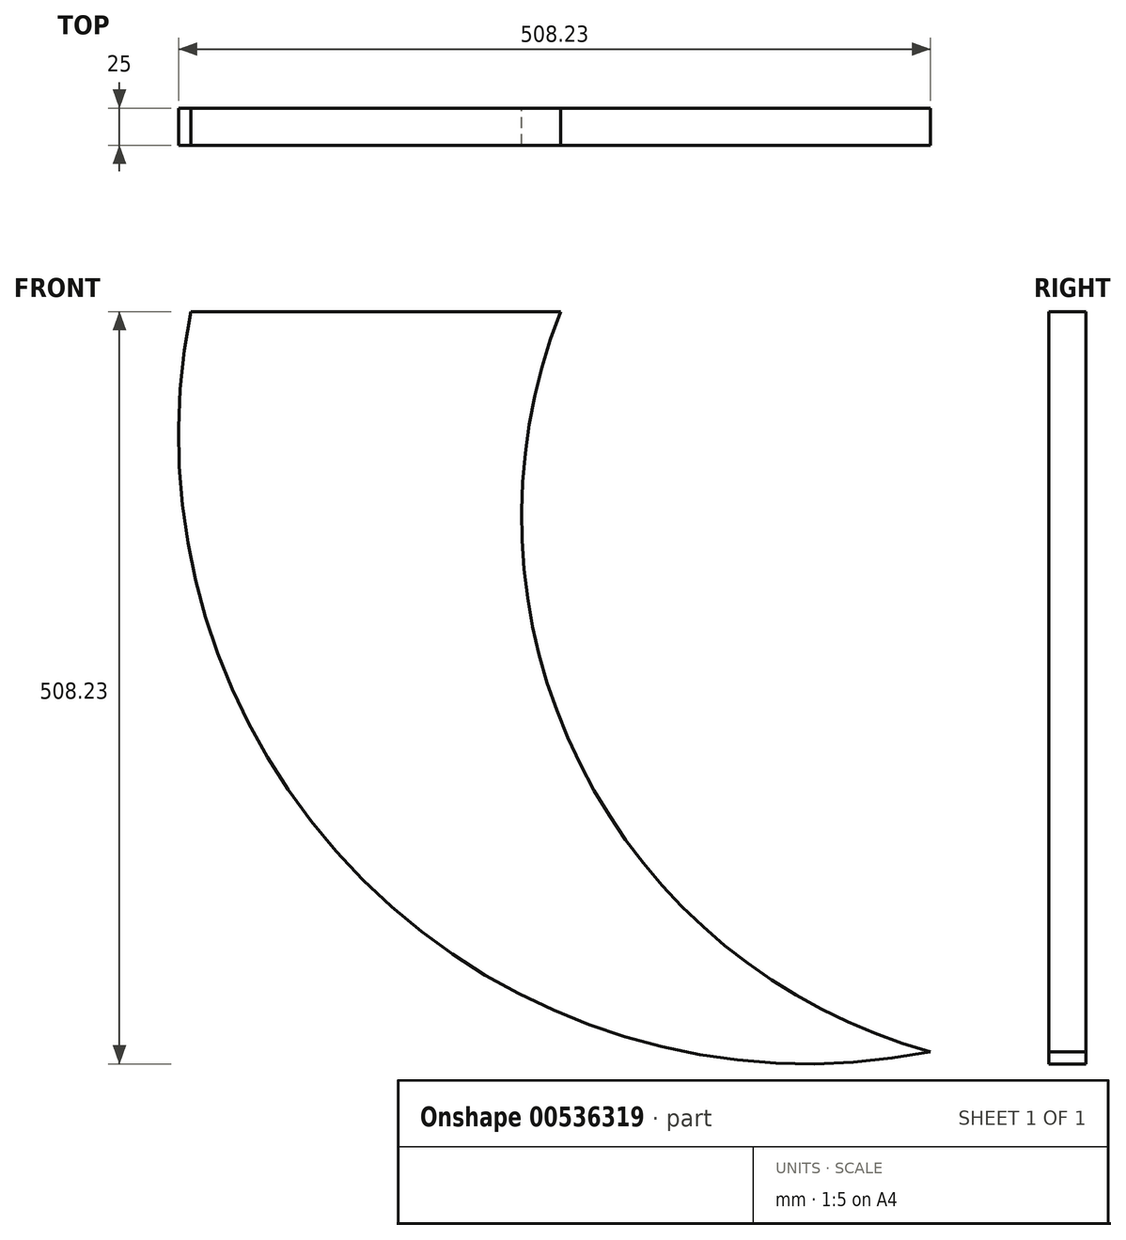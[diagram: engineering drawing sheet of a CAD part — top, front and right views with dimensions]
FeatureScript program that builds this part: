
annotation { "Feature Type Name" : "Feature", "Feature Type Description" : "" }
export const myFeature = defineFeature(function(context is Context, id is Id, definition is map)
    precondition{}
    {
        {
            var Q0;
            Q0=qCreatedBy(makeId("Front.planeOp"),FACE);
            var sketch = newSketch(context, id + "F0", { "sketchPlane" : qUnion([Q0])});
            skLineSegment(sketch, "E0", {"start": v(0, 0) * mm, "end": v(250, 0) * mm});
            skLineSegment(sketch, "E1.bottom", {"start": v(250, 0) * mm, "end": v(500, 0) * mm});
            skLineSegment(sketch, "E1.right", {"start": v(500, 0) * mm, "end": v(500, -500) * mm});
            skArc(sketch, "E2", {"start": v(250, 0) * mm, "mid": v(263.2, -305.9) * mm, "end": v(500, -500) * mm});
            skArc(sketch, "E3", {"start": v(0, 0) * mm, "mid": v(116.25, -383.75) * mm, "end": v(500, -500) * mm});
            skSolve(sketch);
        }
        {
            var Q0;
            {var subQ0=sQuery(id+"F0.wireOp",EDGE,"8YUXyNvU-ZrVt-5ebB-YRxW-zHFFSydLwLN8");Q0=makeQuery(id+"F0.imprint","IMPRINT",FACE,{"disambiguationData":[TD([[makeQuery(id+"F0.imprint","IMPRINT",EDGE,{"derivedFrom":subQ0}),-1.0]])]});}
            var Q1;
            Q1=makeQuery(id+"F0.imprint","IMPRINT",FACE,{"disambiguationData":[TD([[makeQuery(id+"F0.imprint","IMPRINT",EDGE,{"derivedFrom":sQuery(id+"F0.wireOp",EDGE,"E0")}),-1.0]])]});
            extrude(context, id + "F1", {"entities" : qUnion([Q0, Q1]), "depth" : 25 * mm, "offsetDistance" : 25 * mm});
        }
    });
